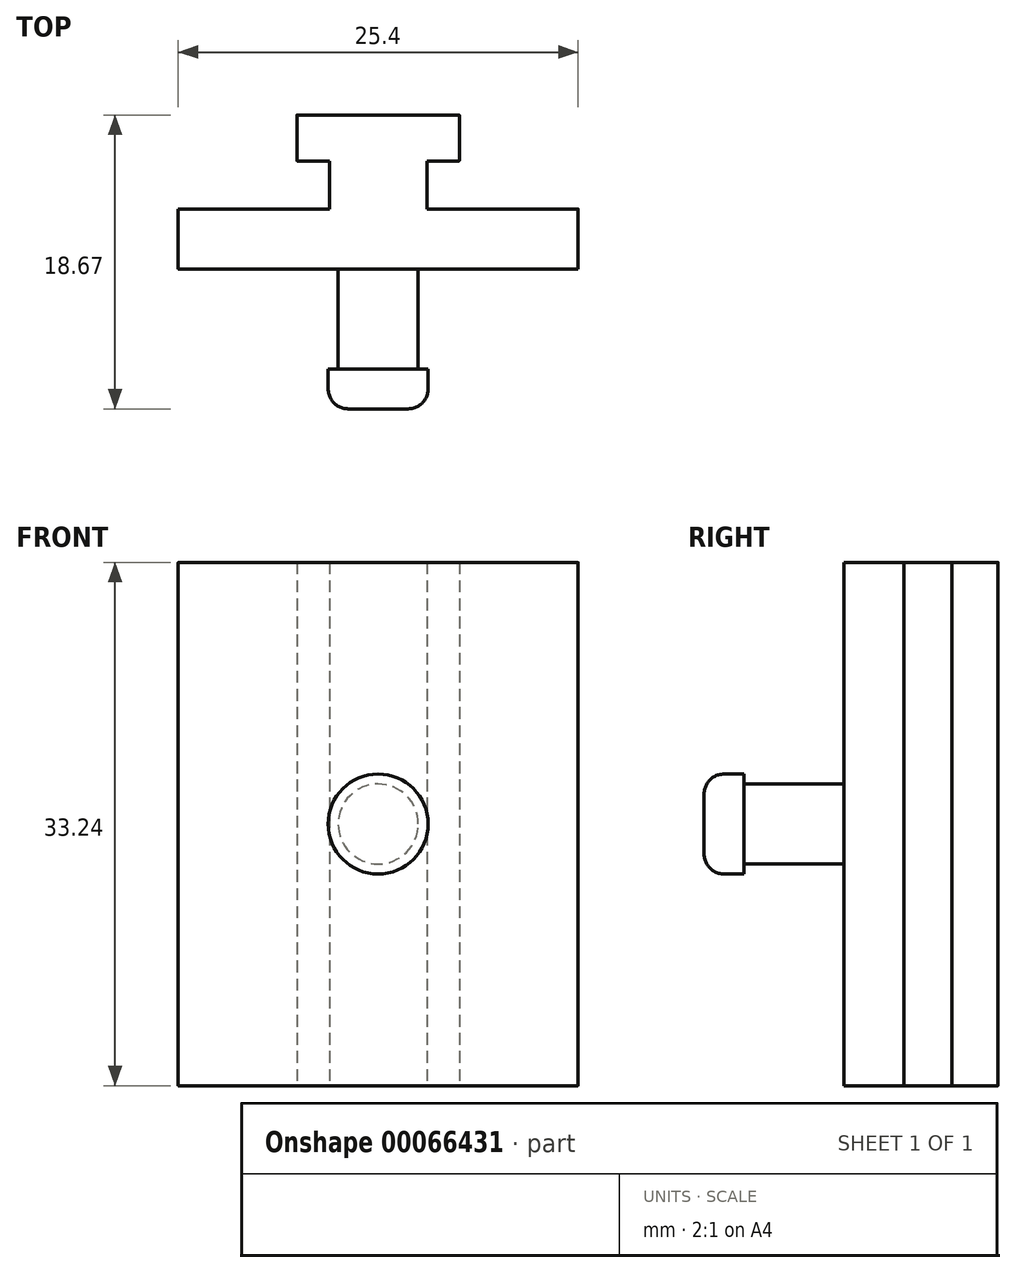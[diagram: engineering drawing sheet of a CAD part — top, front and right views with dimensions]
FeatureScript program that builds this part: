
annotation { "Feature Type Name" : "Feature", "Feature Type Description" : "" }
export const myFeature = defineFeature(function(context is Context, id is Id, definition is map)
    precondition{}
    {
        {
            var Q0;
            Q0=qCreatedBy(makeId("Front.planeOp"),FACE);
            var sketch = newSketch(context, id + "F0", { "sketchPlane" : qUnion([Q0])});
            skLineSegment(sketch, "E0.rect.bottom", {"start": v(5.16, 16.62) * mm, "end": v(-5.16, 16.62) * mm});
            skLineSegment(sketch, "E0.rect.top", {"start": v(5.16, -16.62) * mm, "end": v(-5.16, -16.62) * mm});
            skLineSegment(sketch, "E0.rect.left", {"start": v(5.16, 16.62) * mm, "end": v(5.16, -16.62) * mm});
            skLineSegment(sketch, "E0.rect.right", {"start": v(-5.16, 16.62) * mm, "end": v(-5.16, -16.62) * mm});
            skPoint(sketch, "E0.rect.middle", {"position": v(0, 0) * mm});
            skSolve(sketch);
        }
        {
            var Q0;
            Q0=qSketchRegion(id+"F0",true);
            extrude(context, id + "F1", {"entities" : qUnion([Q0]), "depth" : 2.92 * mm, "offsetDistance" : 25.4 * mm});
        }
        {
            var Q0;
            Q0=makeQuery(id+"F1.opExtrude","CAP_FACE",FACE,{"disambiguationData":[OSD([sQuery(id+"F0.wireOp",EDGE,"E0.rect.bottom"),sQuery(id+"F0.wireOp",EDGE,"E0.rect.top"),sQuery(id+"F0.wireOp",EDGE,"E0.rect.left"),sQuery(id+"F0.wireOp",EDGE,"E0.rect.right")])],"isStart":false});
            var sketch = newSketch(context, id + "F2", { "sketchPlane" : qUnion([Q0])});
            skLineSegment(sketch, "E1.rect.bottom", {"start": v(3.1, 16.62) * mm, "end": v(-3.1, 16.62) * mm});
            skLineSegment(sketch, "E1.rect.top", {"start": v(3.1, -16.62) * mm, "end": v(-3.1, -16.62) * mm});
            skLineSegment(sketch, "E1.rect.left", {"start": v(3.1, 16.62) * mm, "end": v(3.1, -16.62) * mm});
            skLineSegment(sketch, "E1.rect.right", {"start": v(-3.1, 16.62) * mm, "end": v(-3.1, -16.62) * mm});
            skPoint(sketch, "E1.rect.middle", {"position": v(0, 0) * mm});
            skSolve(sketch);
        }
        {
            var Q0;
            Q0=qSketchRegion(id+"F2",true);
            extrude(context, id + "F3", {"entities" : qUnion([Q0]), "operationType" : NewBodyOperationType.ADD, "depth" : 3.05 * mm, "offsetDistance" : 25.4 * mm});
        }
        {
            var Q0;
            Q0=makeQuery(id+"F3.opExtrude","CAP_FACE",FACE,{"disambiguationData":[OSD([sQuery(id+"F2.wireOp",EDGE,"E1.rect.bottom"),sQuery(id+"F2.wireOp",EDGE,"E1.rect.top"),sQuery(id+"F2.wireOp",EDGE,"E1.rect.left"),sQuery(id+"F2.wireOp",EDGE,"E1.rect.right")])],"isStart":false});
            var sketch = newSketch(context, id + "F4", { "sketchPlane" : qUnion([Q0])});
            skLineSegment(sketch, "E2.bottom", {"start": v(-12.7, -16.62) * mm, "end": v(12.7, -16.62) * mm});
            skLineSegment(sketch, "E2.top", {"start": v(-12.7, 16.62) * mm, "end": v(12.7, 16.62) * mm});
            skLineSegment(sketch, "E2.left", {"start": v(-12.7, -16.62) * mm, "end": v(-12.7, 16.62) * mm});
            skLineSegment(sketch, "E2.right", {"start": v(12.7, -16.62) * mm, "end": v(12.7, 16.62) * mm});
            skPoint(sketch, "E3", {"position": v(7.87, 0) * mm});
            skSolve(sketch);
        }
        {
            var Q0;
            Q0=qSketchRegion(id+"F4",true);
            extrude(context, id + "F5", {"entities" : qUnion([Q0]), "operationType" : NewBodyOperationType.ADD, "depth" : 3.8 * mm, "offsetDistance" : 25.4 * mm});
        }
        {
            var Q0;
            Q0=makeQuery(id+"F1.opExtrude","CAP_EDGE",EDGE,{"disambiguationData":[OSD([sQuery(id+"F0.wireOp",EDGE,"E0.rect.left")])],"isStart":false});
            var Q1;
            Q1=makeQuery(id+"F1.opExtrude","CAP_EDGE",EDGE,{"disambiguationData":[OSD([sQuery(id+"F0.wireOp",EDGE,"E0.rect.left")])],"isStart":true});
            var Q2;
            Q2=makeQuery(id+"F1.opExtrude","CAP_EDGE",EDGE,{"disambiguationData":[OSD([sQuery(id+"F0.wireOp",EDGE,"E0.rect.right")])],"isStart":false});
            var Q3;
            Q3=makeQuery(id+"F1.opExtrude","CAP_EDGE",EDGE,{"disambiguationData":[OSD([sQuery(id+"F0.wireOp",EDGE,"E0.rect.right")])],"isStart":true});
            var Q4;
            Q4=makeQuery(id+"F1.opExtrude","CAP_EDGE",EDGE,{"disambiguationData":[OSD([sQuery(id+"F0.wireOp",EDGE,"E0.rect.top")])],"isStart":true});
            var Q5;
            Q5=makeQuery(id+"F1.opExtrude","CAP_EDGE",EDGE,{"disambiguationData":[OSD([sQuery(id+"F0.wireOp",EDGE,"E0.rect.bottom")])],"isStart":true});
            var Q6;
            Q6=makeQuery(id+"F5.opExtrude","SWEPT_EDGE",EDGE,{"disambiguationData":[OSD([sQuery(id+"F4.wireOp",EDGE,"E2.bottom"),sQuery(id+"F4.wireOp",EDGE,"E2.right")])]});
            var Q7;
            Q7=makeQuery(id+"F5.opExtrude","SWEPT_EDGE",EDGE,{"disambiguationData":[OSD([sQuery(id+"F4.wireOp",EDGE,"E2.bottom"),sQuery(id+"F4.wireOp",EDGE,"E2.left")])]});
            var Q8;
            Q8=makeQuery(id+"F5.opExtrude","SWEPT_EDGE",EDGE,{"disambiguationData":[OSD([sQuery(id+"F4.wireOp",EDGE,"E2.top"),sQuery(id+"F4.wireOp",EDGE,"E2.left")])]});
            var Q9;
            Q9=makeQuery(id+"F5.opExtrude","SWEPT_EDGE",EDGE,{"disambiguationData":[OSD([sQuery(id+"F4.wireOp",EDGE,"E2.top"),sQuery(id+"F4.wireOp",EDGE,"E2.right")])]});
            fillet(context, id + "F6", {"entities" : qUnion([Q0, Q1, Q2, Q3, Q4, Q5, Q6, Q7, Q8, Q9]), "radius" : .63 / 50.8 * mm, "tangentPropagation" : true, "allowEdgeOverflow" : false});
        }
        {
            var Q0;
            Q0=makeQuery(id+"F5.opExtrude","CAP_FACE",FACE,{"disambiguationData":[OSD([sQuery(id+"F4.wireOp",EDGE,"E2.bottom"),sQuery(id+"F4.wireOp",EDGE,"E2.top"),sQuery(id+"F4.wireOp",EDGE,"E2.left"),sQuery(id+"F4.wireOp",EDGE,"E2.right")])],"isStart":false});
            var sketch = newSketch(context, id + "F7", { "sketchPlane" : qUnion([Q0])});
            skCircle(sketch, "E4", {"center": v(0, 0) * mm, "radius": 2.54 * mm});
            skSolve(sketch);
        }
        {
            var Q0;
            Q0 = qSketchRegion(id + "F7", true);
            extrude(context, id + "F8", {"entities" : qUnion([Q0]), "operationType" : NewBodyOperationType.ADD, "depth" : 6.35 * mm, "offsetDistance" : 25.4 * mm});
        }
        {
            var Q0;
            Q0=makeQuery(id+"F8.opExtrude","CAP_FACE",FACE,{"disambiguationData":[OSD([sQuery(id+"F7.wireOp",EDGE,"E4")])],"isStart":false});
            var sketch = newSketch(context, id + "F9", { "sketchPlane" : qUnion([Q0])});
            skCircle(sketch, "E5", {"center": v(0, 0) * mm, "radius": 3.18 * mm});
            skSolve(sketch);
        }
        {
            var Q0;
            Q0 = qSketchRegion(id + "F9", true);
            extrude(context, id + "F10", {"entities" : qUnion([Q0]), "operationType" : NewBodyOperationType.ADD, "depth" : 2.54 * mm, "offsetDistance" : 25.4 * mm});
        }
        {
            var Q0;
            Q0=makeQuery(id+"F8.opExtrude","CAP_EDGE",EDGE,{"disambiguationData":[OSD([sQuery(id+"F7.wireOp",EDGE,"E4")])],"isStart":true});
            var Q1;
            Q1=makeQuery(id+"F10.opExtrude","CAP_EDGE",EDGE,{"disambiguationData":[OSD([sQuery(id+"F9.wireOp",EDGE,"E5")])],"isStart":false});
            fillet(context, id + "F11", {"entities" : qUnion([Q0, Q1]), "radius" : 1.27 * mm, "tangentPropagation" : true, "allowEdgeOverflow" : false});
        }
    });
